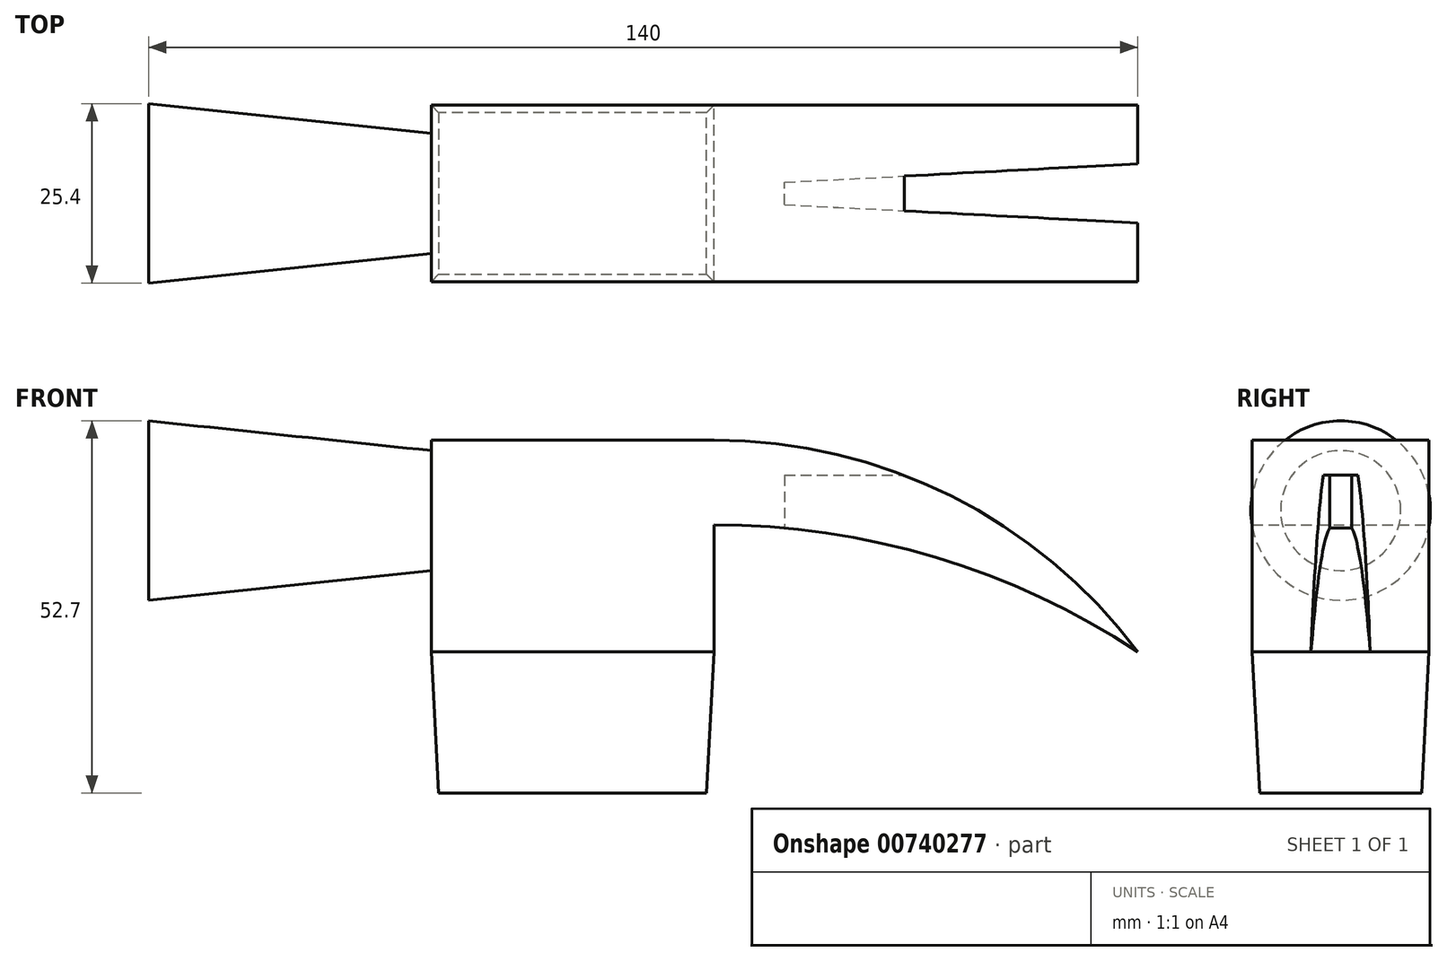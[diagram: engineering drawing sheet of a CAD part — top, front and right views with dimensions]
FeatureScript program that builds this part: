
annotation { "Feature Type Name" : "Feature", "Feature Type Description" : "" }
export const myFeature = defineFeature(function(context is Context, id is Id, definition is map)
    precondition{}
    {
        {
            var Q0;
            Q0=qCreatedBy(makeId("Front.planeOp"),FACE);
            var sketch = newSketch(context, id + "F0", { "sketchPlane" : qUnion([Q0])});
            skLineSegment(sketch, "E0.0", {"start": v(-20, 0) * mm, "end": v(-20, 30) * mm});
            skLineSegment(sketch, "E1.0", {"start": v(20, 0) * mm, "end": v(20, 30) * mm});
            skLineSegment(sketch, "E2", {"start": v(-20, 0) * mm, "end": v(20, 0) * mm});
            skLineSegment(sketch, "E3.0", {"start": v(-20, 30) * mm, "end": v(20, 30) * mm});
            skSolve(sketch);
        }
        {
            var Q0;
            Q0=qSketchRegion(id+"F0",true);
            extrude(context, id + "F1", {"entities" : qUnion([Q0]), "endBound" : BoundingType.SYMMETRIC, "depth" : 25 * mm, "offsetDistance" : 25 * mm});
        }
        {
            var Q0;
            Q0=makeQuery(id+"F1.opExtrude","SWEPT_FACE",FACE,{"disambiguationData":[OSD([sQuery(id+"F0.wireOp",EDGE,"E0.0")])]});
            var sketch = newSketch(context, id + "F2", { "sketchPlane" : qUnion([Q0])});
            skCircle(sketch, "E4", {"center": v(0, 20) * mm, "radius": 8.5 * mm});
            skSolve(sketch);
        }
        {
            var Q0;
            Q0=qSketchRegion(id+"F2",true);
            extrude(context, id + "F3", {"entities" : qUnion([Q0]), "operationType" : NewBodyOperationType.ADD, "depth" : 40 * mm, "offsetDistance" : 25 * mm, "hasDraft" : true, "draftAngle" : 6 * degree});
        }
        {
            var Q0;
            Q0=qCreatedBy(makeId("Front.planeOp"),FACE);
            var sketch = newSketch(context, id + "F4", { "sketchPlane" : qUnion([Q0])});
            skArc(sketch, "E5", {"start": v(80, 0) * mm, "mid": v(53.54, 22.08) * mm, "end": v(20, 30) * mm});
            skArc(sketch, "E6", {"start": v(80, 0) * mm, "mid": v(51.32, 13.4) * mm, "end": v(20, 18) * mm});
            skLineSegment(sketch, "E7", {"start": v(20, 30) * mm, "end": v(20, 18) * mm});
            skSolve(sketch);
        }
        {
            var Q0;
            Q0=qSketchRegion(id+"F4",true);
            extrude(context, id + "F5", {"entities" : qUnion([Q0]), "operationType" : NewBodyOperationType.ADD, "endBound" : BoundingType.SYMMETRIC, "depth" : 25 * mm, "offsetDistance" : 25 * mm});
        }
        {
            var Q0;
            Q0=makeQuery(id+"F1.opExtrude","SWEPT_FACE",FACE,{"disambiguationData":[OSD([sQuery(id+"F0.wireOp",EDGE,"E2")])]});
            extrude(context, id + "F6", {"entities" : qUnion([Q0]), "depth" : 20 * mm, "offsetDistance" : 25 * mm, "hasDraft" : true, "draftAngle" : 3 * degree, "draftPullDirection" : true});
        }
        {
            var Q0;
            Q0=qCreatedBy(makeId("Top.planeOp"),FACE);
            var sketch = newSketch(context, id + "F7", { "sketchPlane" : qUnion([Q0])});
            skLineSegment(sketch, "E8", {"start": v(30, 1.57) * mm, "end": v(98.1, 5.14) * mm});
            skLineSegment(sketch, "E9", {"start": v(30, -1.57) * mm, "end": v(98.1, -5.14) * mm});
            skLineSegment(sketch, "E10", {"start": v(98.1, -5.14) * mm, "end": v(98.1, 5.14) * mm});
            skLineSegment(sketch, "E11.0", {"start": v(30, -1.57) * mm, "end": v(30, 1.57) * mm});
            skSolve(sketch);
        }
        {
            var Q0;
            Q0=qSketchRegion(id+"F7",true);
            extrude(context, id + "F8", {"entities" : qUnion([Q0]), "operationType" : NewBodyOperationType.REMOVE, "depth" : 25 * mm, "offsetDistance" : 25 * mm});
        }
    });
